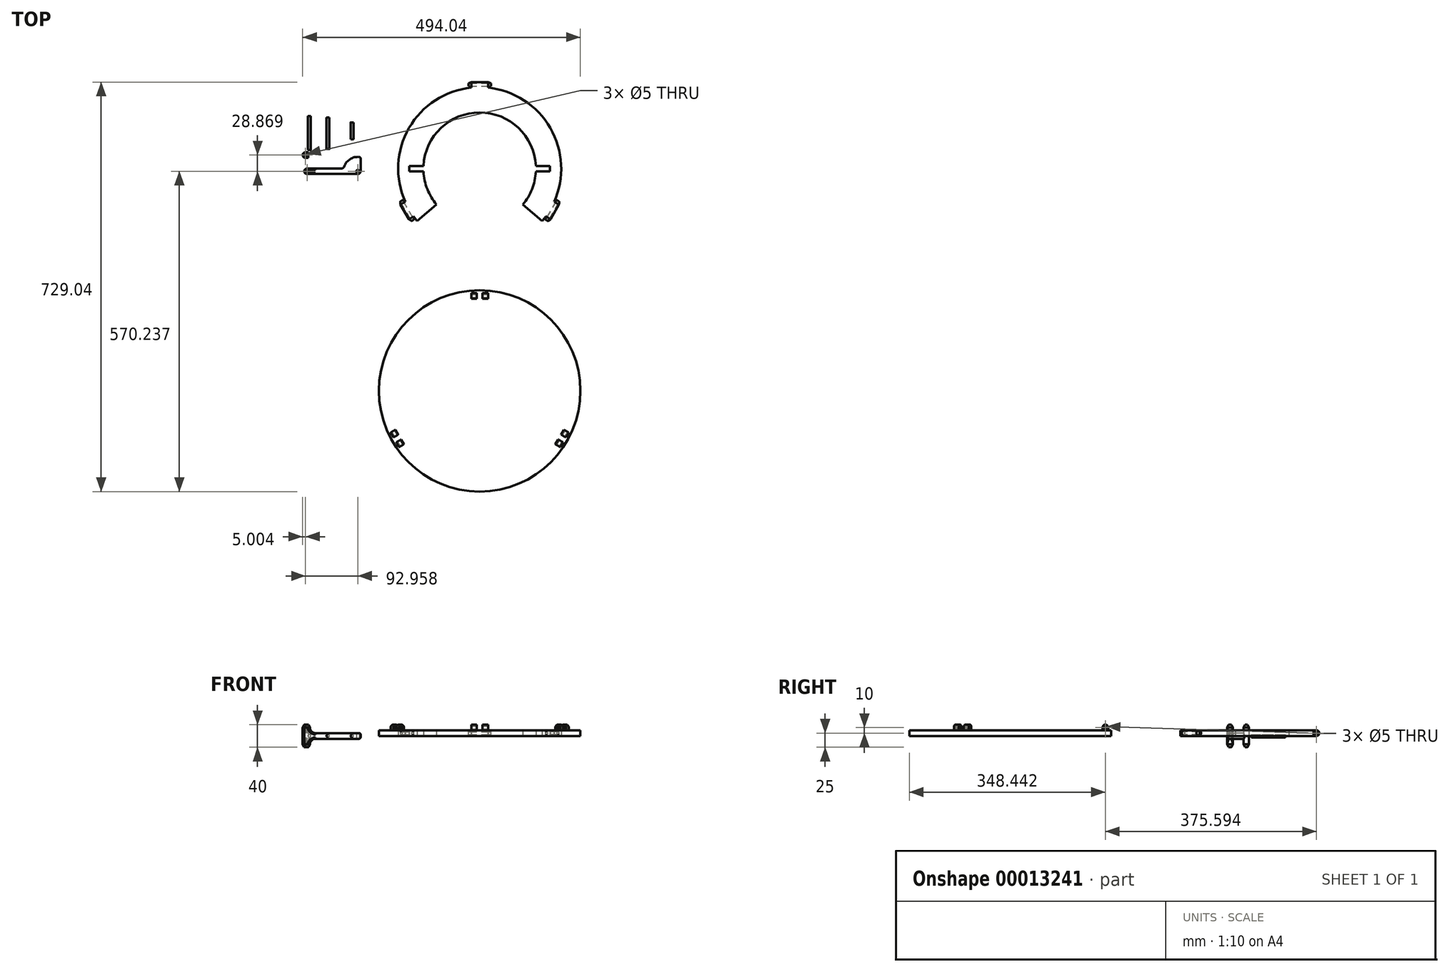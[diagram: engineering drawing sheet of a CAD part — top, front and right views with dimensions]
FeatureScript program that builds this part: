
annotation { "Feature Type Name" : "Feature", "Feature Type Description" : "" }
export const myFeature = defineFeature(function(context is Context, id is Id, definition is map)
    precondition{}
    {
        {
            var Q0;
            Q0=qCreatedBy(makeId("Top.planeOp"),FACE);
            var sketch = newSketch(context, id + "F0", { "sketchPlane" : qUnion([Q0])});
            skCircle(sketch, "E0", {"center": v(-58.2, 42.53) * mm, "radius": 2.5 * mm});
            skLineSegment(sketch, "E1", {"start": v(-53.2, 37.53) * mm, "end": v(-58.2, 37.53) * mm, "construction": true});
            skLineSegment(sketch, "E2", {"start": v(-148.2, 37.53) * mm, "end": v(-148.2, 47.53) * mm, "construction": true});
            skLineSegment(sketch, "E3", {"start": v(-148.2, 47.53) * mm, "end": v(-83.2, 47.53) * mm});
            skLineSegment(sketch, "E4", {"start": v(-83.2, 47.53) * mm, "end": v(-53.2, 67.53) * mm, "construction": true});
            skLineSegment(sketch, "E5", {"start": v(-53.2, 67.53) * mm, "end": v(-53.2, 42.53) * mm});
            skLineSegment(sketch, "E6", {"start": v(-53.2, 37.53) * mm, "end": v(-58.2, 42.53) * mm, "construction": true});
            skArc(sketch, "E7", {"start": v(-148.2, 47.53) * mm, "mid": v(-153.2, 42.53) * mm, "end": v(-148.2, 37.53) * mm});
            skArc(sketch, "E8", {"start": v(-53.2, 67.53) * mm, "mid": v(-72.34, 63.74) * mm, "end": v(-83.2, 47.53) * mm});
            skLineSegment(sketch, "E9", {"start": v(-148.2, 42.53) * mm, "end": v(-58.2, 42.53) * mm, "construction": true});
            skCircle(sketch, "E10", {"center": v(-148.2, 42.53) * mm, "radius": 2.5 * mm});
            skCircle(sketch, "E11", {"center": v(-148.2, 42.53) * mm, "radius": 5 * mm});
            skArc(sketch, "E12", {"start": v(-53.2, 42.53) * mm, "mid": v(-61.73, 46.06) * mm, "end": v(-58.2, 37.53) * mm, "construction": true});
            skArc(sketch, "E13", {"start": v(-58.2, 37.53) * mm, "mid": v(-54.66, 39) * mm, "end": v(-53.2, 42.53) * mm});
            skLineSegment(sketch, "E14", {"start": v(-53.2, 42.53) * mm, "end": v(-53.2, 37.53) * mm, "construction": true});
            skLineSegment(sketch, "E15", {"start": v(-58.2, 37.53) * mm, "end": v(-148.2, 37.53) * mm});
            skLineSegment(sketch, "E16.bottom", {"start": v(-111.22, 138) * mm, "end": v(-108.72, 138) * mm});
            skLineSegment(sketch, "E16.top", {"start": v(-111.22, 82) * mm, "end": v(-108.72, 82) * mm});
            skLineSegment(sketch, "E16.left", {"start": v(-111.22, 138) * mm, "end": v(-111.22, 82) * mm});
            skLineSegment(sketch, "E16.right", {"start": v(-108.72, 138) * mm, "end": v(-108.72, 82) * mm});
            skLineSegment(sketch, "E17", {"start": v(-148.2, 42.53) * mm, "end": v(-145.7, 42.53) * mm, "construction": true});
            skLineSegment(sketch, "E18", {"start": v(-58.2, 42.53) * mm, "end": v(-55.7, 42.53) * mm, "construction": true});
            skLineSegment(sketch, "E19.bottom", {"start": v(-68.32, 129.56) * mm, "end": v(-65.82, 129.56) * mm});
            skLineSegment(sketch, "E19.top", {"start": v(-68.32, 99.56) * mm, "end": v(-65.82, 99.56) * mm});
            skLineSegment(sketch, "E19.left", {"start": v(-68.32, 129.56) * mm, "end": v(-68.32, 99.56) * mm});
            skLineSegment(sketch, "E19.right", {"start": v(-65.82, 129.56) * mm, "end": v(-65.82, 99.56) * mm});
            skLineSegment(sketch, "E20.bottom", {"start": v(-144.15, 140.66) * mm, "end": v(-141.65, 140.66) * mm});
            skLineSegment(sketch, "E20.top", {"start": v(-144.15, 80.66) * mm, "end": v(-141.65, 80.66) * mm});
            skLineSegment(sketch, "E20.left", {"start": v(-144.15, 140.66) * mm, "end": v(-144.15, 80.66) * mm});
            skLineSegment(sketch, "E20.right", {"start": v(-141.65, 140.66) * mm, "end": v(-141.65, 80.66) * mm});
            skLineSegment(sketch, "E21.bottom", {"start": v(33.66, 52.1) * mm, "end": v(283.66, 52.1) * mm, "construction": true});
            skLineSegment(sketch, "E21.top", {"start": v(33.66, 42.1) * mm, "end": v(283.66, 42.1) * mm, "construction": true});
            skLineSegment(sketch, "E21.left", {"start": v(33.66, 52.1) * mm, "end": v(33.66, 42.1) * mm, "construction": true});
            skLineSegment(sketch, "E21.right", {"start": v(283.66, 52.1) * mm, "end": v(283.66, 42.1) * mm, "construction": true});
            skPoint(sketch, "E22", {"position": v(158.66, 47.1) * mm});
            skCircle(sketch, "E23", {"center": v(158.66, 47.1) * mm, "radius": 100 * mm});
            skCircle(sketch, "E24.cCircle", {"center": v(158.66, 47.1) * mm, "radius": 125.1 * mm, "construction": true});
            skCircle(sketch, "E25", {"center": v(158.66, 47.1) * mm, "radius": 145 * mm});
            skLineSegment(sketch, "E26", {"start": v(158.66, 47.1) * mm, "end": v(158.66, 192.1) * mm, "construction": true});
            skLineSegment(sketch, "E27", {"start": v(158.66, 47.1) * mm, "end": v(284.23, -25.4) * mm, "construction": true});
            skLineSegment(sketch, "E28", {"start": v(33.08, -25.4) * mm, "end": v(158.66, 47.1) * mm, "construction": true});
            skLineSegment(sketch, "E29.bottom", {"start": v(143.66, 201.33) * mm, "end": v(173.66, 201.33) * mm});
            skLineSegment(sketch, "E29.top", {"start": v(143.66, 191.33) * mm, "end": v(173.66, 191.33) * mm, "construction": true});
            skLineSegment(sketch, "E29.left", {"start": v(143.66, 201.33) * mm, "end": v(143.66, 191.33) * mm});
            skLineSegment(sketch, "E29.right", {"start": v(173.66, 201.33) * mm, "end": v(173.66, 191.33) * mm});
            skPoint(sketch, "E30", {"position": v(158.66, 191.33) * mm});
            skLineSegment(sketch, "E31.bottom", {"start": v(26.26, -12.02) * mm, "end": v(41.26, -38) * mm, "construction": true});
            skLineSegment(sketch, "E31.top", {"start": v(17.6, -17.02) * mm, "end": v(32.6, -43) * mm});
            skLineSegment(sketch, "E31.left", {"start": v(26.26, -12.02) * mm, "end": v(17.6, -17.02) * mm});
            skLineSegment(sketch, "E31.right", {"start": v(41.26, -38) * mm, "end": v(32.6, -43) * mm});
            skLineSegment(sketch, "E32.bottom", {"start": v(276.06, -38) * mm, "end": v(291.06, -12.02) * mm, "construction": true});
            skLineSegment(sketch, "E32.top", {"start": v(284.72, -43) * mm, "end": v(299.72, -17.02) * mm});
            skLineSegment(sketch, "E32.left", {"start": v(276.06, -38) * mm, "end": v(284.72, -43) * mm});
            skLineSegment(sketch, "E32.right", {"start": v(291.06, -12.02) * mm, "end": v(299.72, -17.02) * mm});
            skPoint(sketch, "E33", {"position": v(33.76, -25) * mm});
            skPoint(sketch, "E34", {"position": v(283.56, -25) * mm});
            skLineSegment(sketch, "E35", {"start": v(47.4, -45.89) * mm, "end": v(81.93, -17.03) * mm});
            skLineSegment(sketch, "E36", {"start": v(235.38, -17.03) * mm, "end": v(269.91, -45.89) * mm});
            skPoint(sketch, "E37", {"position": v(524.59, -60.45) * mm});
            skLineSegment(sketch, "E38", {"start": v(544.59, 16.73) * mm, "end": v(544.59, 116.73) * mm});
            skLineSegment(sketch, "E39", {"start": v(524.59, -60.45) * mm, "end": v(453.2, -60.45) * mm, "construction": true});
            skLineSegment(sketch, "E40", {"start": v(524.59, -60.45) * mm, "end": v(456.48, -1.62) * mm, "construction": true});
            skLineSegment(sketch, "E41", {"start": v(456.48, -1.62) * mm, "end": v(544.59, 16.73) * mm, "construction": true});
            skLineSegment(sketch, "E42", {"start": v(524.59, -60.45) * mm, "end": v(522.35, 29.52) * mm, "construction": true});
            skLineSegment(sketch, "E43", {"start": v(522.35, 29.52) * mm, "end": v(544.59, 116.73) * mm, "construction": true});
            skCircle(sketch, "E44", {"center": v(-151.16, 71.4) * mm, "radius": 5 * mm});
            skCircle(sketch, "E45", {"center": v(-151.16, 71.4) * mm, "radius": 2.5 * mm});
            skLineSegment(sketch, "E46.bottom", {"start": v(-151.16, 76.4) * mm, "end": v(-146.16, 76.4) * mm});
            skLineSegment(sketch, "E46.top", {"start": v(-151.16, 66.4) * mm, "end": v(-146.16, 66.4) * mm});
            skLineSegment(sketch, "E46.left", {"start": v(-151.16, 76.4) * mm, "end": v(-151.16, 66.4) * mm, "construction": true});
            skLineSegment(sketch, "E46.right", {"start": v(-146.16, 76.4) * mm, "end": v(-146.16, 66.4) * mm});
            skLineSegment(sketch, "E47", {"start": v(58.78, 52.1) * mm, "end": v(33.66, 52.1) * mm});
            skLineSegment(sketch, "E48", {"start": v(58.78, 42.1) * mm, "end": v(33.66, 42.1) * mm});
            skLineSegment(sketch, "E49", {"start": v(33.66, 42.1) * mm, "end": v(33.66, 52.1) * mm});
            skLineSegment(sketch, "E50", {"start": v(258.53, 52.1) * mm, "end": v(283.66, 52.1) * mm});
            skLineSegment(sketch, "E51", {"start": v(283.66, 42.1) * mm, "end": v(283.66, 52.1) * mm});
            skLineSegment(sketch, "E52", {"start": v(283.66, 42.1) * mm, "end": v(258.53, 42.1) * mm});
            skCircle(sketch, "E53", {"center": v(158.66, -348.5) * mm, "radius": 179.22 * mm});
            skLineSegment(sketch, "E54", {"start": v(143.66, 196.33) * mm, "end": v(173.66, 196.33) * mm, "construction": true});
            skLineSegment(sketch, "E55", {"start": v(158.66, 47.1) * mm, "end": v(158.66, 196.33) * mm, "construction": true});
            skLineSegment(sketch, "E56", {"start": v(158.66, -348.5) * mm, "end": v(158.66, -169.27) * mm, "construction": true});
            skLineSegment(sketch, "E57", {"start": v(143.66, -179.27) * mm, "end": v(173.66, -179.27) * mm, "construction": true});
            skLineSegment(sketch, "E58.bottom", {"start": v(143.66, -174.27) * mm, "end": v(153.66, -174.27) * mm});
            skLineSegment(sketch, "E58.top", {"start": v(143.66, -184.27) * mm, "end": v(153.66, -184.27) * mm});
            skLineSegment(sketch, "E58.left", {"start": v(143.66, -174.27) * mm, "end": v(143.66, -184.27) * mm});
            skLineSegment(sketch, "E58.right", {"start": v(153.66, -174.27) * mm, "end": v(153.66, -184.27) * mm});
            skLineSegment(sketch, "E59.bottom", {"start": v(163.66, -174.27) * mm, "end": v(173.66, -174.27) * mm});
            skLineSegment(sketch, "E59.top", {"start": v(163.66, -184.27) * mm, "end": v(173.66, -184.27) * mm});
            skLineSegment(sketch, "E59.left", {"start": v(163.66, -174.27) * mm, "end": v(163.66, -184.27) * mm});
            skLineSegment(sketch, "E59.right", {"start": v(173.66, -174.27) * mm, "end": v(173.66, -184.27) * mm});
            skPoint(sketch, "E60", {"position": v(158.66, -179.27) * mm});
            skLineSegment(sketch, "E61", {"start": v(158.66, -110.61) * mm, "end": v(307.88, -110.61) * mm, "construction": true});
            skLineSegment(sketch, "E62", {"start": v(307.88, -110.61) * mm, "end": v(327.88, -110.61) * mm, "construction": true});
            skLineSegment(sketch, "E63", {"start": v(524.59, -60.45) * mm, "end": v(544.59, -60.45) * mm, "construction": true});
            skLineSegment(sketch, "E64", {"start": v(158.66, -117.1) * mm, "end": v(327.88, -117.1) * mm, "construction": true});
            skLineSegment(sketch, "E65", {"start": v(158.66, -179.27) * mm, "end": v(158.66, -348.5) * mm, "construction": true});
            skLineSegment(sketch, "E66", {"start": v(158.66, -348.5) * mm, "end": v(305.2, -433.1) * mm, "construction": true});
            skLineSegment(sketch, "E67", {"start": v(12.1, -433.1) * mm, "end": v(158.66, -348.5) * mm, "construction": true});
            skLineSegment(sketch, "E68", {"start": v(297.7, -446.1) * mm, "end": v(312.7, -420.11) * mm, "construction": true});
            skLineSegment(sketch, "E69.bottom", {"start": v(303.38, -426.27) * mm, "end": v(308.38, -417.61) * mm});
            skLineSegment(sketch, "E69.top", {"start": v(312.04, -431.27) * mm, "end": v(317.04, -422.61) * mm});
            skLineSegment(sketch, "E69.left", {"start": v(303.38, -426.27) * mm, "end": v(312.04, -431.27) * mm});
            skLineSegment(sketch, "E69.right", {"start": v(308.38, -417.61) * mm, "end": v(317.04, -422.61) * mm});
            skLineSegment(sketch, "E70.bottom", {"start": v(298.38, -434.93) * mm, "end": v(307.04, -439.93) * mm});
            skLineSegment(sketch, "E70.top", {"start": v(293.38, -443.6) * mm, "end": v(302.04, -448.6) * mm});
            skLineSegment(sketch, "E70.left", {"start": v(298.38, -434.93) * mm, "end": v(293.38, -443.6) * mm});
            skLineSegment(sketch, "E70.right", {"start": v(307.04, -439.93) * mm, "end": v(302.04, -448.6) * mm});
            skLineSegment(sketch, "E71", {"start": v(4.6, -420.11) * mm, "end": v(19.6, -446.1) * mm, "construction": true});
            skLineSegment(sketch, "E72.bottom", {"start": v(18.94, -434.93) * mm, "end": v(23.94, -443.6) * mm});
            skLineSegment(sketch, "E72.top", {"start": v(10.28, -439.93) * mm, "end": v(15.28, -448.6) * mm});
            skLineSegment(sketch, "E72.left", {"start": v(23.94, -443.6) * mm, "end": v(15.28, -448.6) * mm});
            skLineSegment(sketch, "E72.right", {"start": v(18.94, -434.93) * mm, "end": v(10.28, -439.93) * mm});
            skLineSegment(sketch, "E73.bottom", {"start": v(8.94, -417.61) * mm, "end": v(13.94, -426.27) * mm});
            skLineSegment(sketch, "E73.top", {"start": v(0.28, -422.61) * mm, "end": v(5.28, -431.27) * mm});
            skLineSegment(sketch, "E73.left", {"start": v(13.94, -426.27) * mm, "end": v(5.28, -431.27) * mm});
            skLineSegment(sketch, "E73.right", {"start": v(8.94, -417.61) * mm, "end": v(0.28, -422.61) * mm});
            skSolve(sketch);
        }
        {
            var Q0;
            Q0=makeQuery(id+"F0.imprint","IMPRINT",FACE,{"disambiguationData":[TD([[makeQuery(id+"F0.imprint","IMPRINT",EDGE,{"derivedFrom":sQuery(id+"F0.wireOp",EDGE,"E0")}),-1.0]])]});
            var Q1;
            Q1=makeQuery(id+"F0.imprint","IMPRINT",FACE,{"disambiguationData":[TD([[makeQuery(id+"F0.imprint","IMPRINT",EDGE,{"derivedFrom":sQuery(id+"F0.wireOp",EDGE,"E10")}),-1.0]])]});
            extrude(context, id + "F1", {"entities" : qUnion([Q0, Q1]), "endBound" : BoundingType.SYMMETRIC, "depth" : 10 * mm});
        }
        {
            var Q0;
            Q0=makeQuery(id+"F0.imprint","IMPRINT",FACE,{"disambiguationData":[TD([[makeQuery(id+"F0.imprint","IMPRINT",EDGE,{"derivedFrom":sQuery(id+"F0.wireOp",EDGE,"E10")}),-1.0]])]});
            extrude(context, id + "F2", {"entities" : qUnion([Q0]), "operationType" : NewBodyOperationType.ADD, "endBound" : BoundingType.SYMMETRIC, "depth" : 30 * mm});
        }
        {
            var Q0;
            {var subQ0=sQuery(id+"F0.wireOp",EDGE,"E11");Q0=makeQuery(id+"F2.boolean.opBoolean","INTERSECT",EDGE,{"derivedFrom":[makeQuery(id+"F1.opExtrude","CAP_FACE",FACE,{"disambiguationData":[OSD([sQuery(id+"F0.wireOp",EDGE,"E0"),sQuery(id+"F0.wireOp",EDGE,"E3"),sQuery(id+"F0.wireOp",EDGE,"E5"),sQuery(id+"F0.wireOp",EDGE,"E8"),sQuery(id+"F0.wireOp",EDGE,"E10"),subQ0,sQuery(id+"F0.wireOp",EDGE,"E13"),sQuery(id+"F0.wireOp",EDGE,"E15")])],"isStart":false}),makeQuery(id+"F2.opExtrude","SWEPT_FACE",FACE,{"disambiguationData":[OSD([subQ0])]})]});}
            var Q1;
            {var subQ0=sQuery(id+"F0.wireOp",EDGE,"E11");Q1=makeQuery(id+"F2.boolean.opBoolean","INTERSECT",EDGE,{"derivedFrom":[makeQuery(id+"F1.opExtrude","CAP_FACE",FACE,{"disambiguationData":[OSD([sQuery(id+"F0.wireOp",EDGE,"E0"),sQuery(id+"F0.wireOp",EDGE,"E3"),sQuery(id+"F0.wireOp",EDGE,"E5"),sQuery(id+"F0.wireOp",EDGE,"E8"),sQuery(id+"F0.wireOp",EDGE,"E10"),subQ0,sQuery(id+"F0.wireOp",EDGE,"E13"),sQuery(id+"F0.wireOp",EDGE,"E15")])],"isStart":true}),makeQuery(id+"F2.opExtrude","SWEPT_FACE",FACE,{"disambiguationData":[OSD([subQ0])]})]});}
            fillet(context, id + "F3", {"entities" : qUnion([Q0, Q1]), "radius" : 10 * mm, "allowEdgeOverflow" : false});
        }
        {
            var Q0;
            Q0=makeQuery(id+"F1.opExtrude","SWEPT_EDGE",EDGE,{"disambiguationData":[OSD([sQuery(id+"F0.wireOp",EDGE,"E3"),sQuery(id+"F0.wireOp",EDGE,"E8")])]});
            fillet(context, id + "F4", {"entities" : qUnion([Q0]), "radius" : 5 * mm, "tangentPropagation" : true, "allowEdgeOverflow" : false});
        }
        {
            var Q0;
            Q0=makeQuery(id+"F1.opExtrude","CAP_EDGE",EDGE,{"disambiguationData":[OSD([sQuery(id+"F0.wireOp",EDGE,"E15")])],"isStart":false});
            var Q1;
            Q1=makeQuery(id+"F1.opExtrude","CAP_EDGE",EDGE,{"disambiguationData":[OSD([sQuery(id+"F0.wireOp",EDGE,"E8")])],"isStart":false});
            var Q2;
            Q2=makeQuery(id+"F1.opExtrude","CAP_EDGE",EDGE,{"disambiguationData":[OSD([sQuery(id+"F0.wireOp",EDGE,"E15")])],"isStart":true});
            var Q3;
            Q3=makeQuery(id+"F1.opExtrude","CAP_EDGE",EDGE,{"disambiguationData":[OSD([sQuery(id+"F0.wireOp",EDGE,"E3")])],"isStart":true});
            var Q4;
            Q4=makeQuery(id+"F1.opExtrude","SWEPT_EDGE",EDGE,{"disambiguationData":[OSD([sQuery(id+"F0.wireOp",EDGE,"E5"),sQuery(id+"F0.wireOp",EDGE,"E8")])]});
            fillet(context, id + "F5", {"entities" : qUnion([Q0, Q1, Q2, Q3, Q4]), "radius" : 2.5 * mm, "tangentPropagation" : true, "allowEdgeOverflow" : false});
        }
        {
            var Q0;
            Q0=makeQuery(id+"F2.opExtrude","CAP_FACE",FACE,{"disambiguationData":[OSD([sQuery(id+"F0.wireOp",EDGE,"E10"),sQuery(id+"F0.wireOp",EDGE,"E11")])],"isStart":false});
            extrude(context, id + "F6", {"entities" : qUnion([Q0]), "operationType" : NewBodyOperationType.ADD, "depth" : 5 * mm});
        }
        {
            var Q0;
            Q0=makeQuery(id+"F2.opExtrude","CAP_FACE",FACE,{"disambiguationData":[OSD([sQuery(id+"F0.wireOp",EDGE,"E10"),sQuery(id+"F0.wireOp",EDGE,"E11")])],"isStart":true});
            extrude(context, id + "F7", {"entities" : qUnion([Q0]), "operationType" : NewBodyOperationType.ADD, "depth" : 5 * mm});
        }
        {
            var Q0;
            Q0=makeQuery(id+"F6.opExtrude","CAP_EDGE",EDGE,{"disambiguationData":[OSD([sQuery(id+"F0.wireOp",EDGE,"E0"),sQuery(id+"F0.wireOp",EDGE,"E3"),sQuery(id+"F0.wireOp",EDGE,"E5"),sQuery(id+"F0.wireOp",EDGE,"E8"),sQuery(id+"F0.wireOp",EDGE,"E10"),sQuery(id+"F0.wireOp",EDGE,"E11"),sQuery(id+"F0.wireOp",EDGE,"E13"),sQuery(id+"F0.wireOp",EDGE,"E15")])],"isStart":false});
            var Q1;
            Q1=makeQuery(id+"F7.opExtrude","CAP_EDGE",EDGE,{"disambiguationData":[OSD([sQuery(id+"F0.wireOp",EDGE,"E0"),sQuery(id+"F0.wireOp",EDGE,"E3"),sQuery(id+"F0.wireOp",EDGE,"E5"),sQuery(id+"F0.wireOp",EDGE,"E8"),sQuery(id+"F0.wireOp",EDGE,"E10"),sQuery(id+"F0.wireOp",EDGE,"E11"),sQuery(id+"F0.wireOp",EDGE,"E13"),sQuery(id+"F0.wireOp",EDGE,"E15")])],"isStart":false});
            chamfer(context, id + "F8", {"entities" : qUnion([Q0, Q1]), "chamferType" : ChamferType.TWO_OFFSETS, "width1" : 2.5 * mm, "oppositeDirection" : false, "width2" : 5 * mm, "tangentPropagation" : true});
        }
        {
            var Q0;
            Q0=makeQuery(id+"F0.imprint","IMPRINT",FACE,{"disambiguationData":[TD([[makeQuery(id+"F0.imprint","IMPRINT",EDGE,{"derivedFrom":sQuery(id+"F0.wireOp",EDGE,"E20.bottom")}),-1.0]])]});
            var Q1;
            Q1=sQuery(id+"F0.wireOp",EDGE,"E20.left");
            revolve(context, id + "F9", {"entities" : qUnion([Q0]), "axis" : qUnion([Q1]), "revolveType" : RevolveType.FULL});
        }
        {
            var Q0;
            Q0=makeQuery(id+"F0.imprint","IMPRINT",FACE,{"disambiguationData":[TD([[makeQuery(id+"F0.imprint","IMPRINT",EDGE,{"derivedFrom":sQuery(id+"F0.wireOp",EDGE,"E16.bottom")}),-1.0]])]});
            var Q1;
            Q1=sQuery(id+"F0.wireOp",EDGE,"E16.left");
            revolve(context, id + "F10", {"entities" : qUnion([Q0]), "axis" : qUnion([Q1]), "revolveType" : RevolveType.FULL});
        }
        {
            var Q0;
            Q0=makeQuery(id+"F0.imprint","IMPRINT",FACE,{"disambiguationData":[TD([[makeQuery(id+"F0.imprint","IMPRINT",EDGE,{"derivedFrom":sQuery(id+"F0.wireOp",EDGE,"E19.bottom")}),-1.0]])]});
            var Q1;
            Q1=sQuery(id+"F0.wireOp",EDGE,"E19.left");
            revolve(context, id + "F11", {"entities" : qUnion([Q0]), "axis" : qUnion([Q1]), "revolveType" : RevolveType.FULL});
        }
        {
            var Q0;
            Q0=makeQuery(id+"F0.imprint","IMPRINT",FACE,{"disambiguationData":[TD([[makeQuery(id+"F0.imprint","IMPRINT",EDGE,{"derivedFrom":sQuery(id+"F0.wireOp",EDGE,"E45")}),-1.0]])]});
            var Q1;
            {var subQ3=sQuery(id+"F0.wireOp",EDGE,"E46.top");Q1=makeQuery(id+"F0.imprint","IMPRINT",FACE,{"disambiguationData":[TD([[makeQuery(id+"F0.imprint","IMPRINT",EDGE,{"derivedFrom":subQ3}),1.0]])]});}
            var Q2;
            {var subQ3=sQuery(id+"F0.wireOp",EDGE,"E46.bottom");Q2=makeQuery(id+"F0.imprint","IMPRINT",FACE,{"disambiguationData":[TD([[makeQuery(id+"F0.imprint","IMPRINT",EDGE,{"derivedFrom":subQ3}),-1.0]])]});}
            extrude(context, id + "F12", {"entities" : qUnion([Q0, Q1, Q2]), "endBound" : BoundingType.SYMMETRIC, "depth" : 30 * mm});
        }
        {
            var Q0;
            Q0=makeQuery(id+"F0.imprint","IMPRINT",FACE,{"disambiguationData":[TD([[makeQuery(id+"F0.imprint","IMPRINT",EDGE,{"derivedFrom":sQuery(id+"F0.wireOp",EDGE,"E45")}),-1.0]])]});
            extrude(context, id + "F13", {"entities" : qUnion([Q0]), "operationType" : NewBodyOperationType.ADD, "endBound" : BoundingType.SYMMETRIC, "depth" : 40 * mm});
        }
        {
            var Q0;
            Q0=makeQuery(id+"F13.opExtrude","CAP_EDGE",EDGE,{"disambiguationData":[OSD([sQuery(id+"F0.wireOp",EDGE,"E44")])],"isStart":true});
            var Q1;
            Q1=makeQuery(id+"F13.opExtrude","CAP_EDGE",EDGE,{"disambiguationData":[OSD([sQuery(id+"F0.wireOp",EDGE,"E44")])],"isStart":false});
            chamfer(context, id + "F14", {"entities" : qUnion([Q0, Q1]), "chamferType" : ChamferType.TWO_OFFSETS, "width1" : 2.6 * mm, "oppositeDirection" : true, "width2" : 5 * mm, "tangentPropagation" : true});
        }
        {
            var Q0;
            Q0=makeQuery(id+"F0.imprint","IMPRINT",FACE,{"disambiguationData":[TD([[makeQuery(id+"F0.imprint","IMPRINT",EDGE,{"derivedFrom":sQuery(id+"F0.wireOp",EDGE,"E53")}),1.0]])]});
            extrude(context, id + "F15", {"entities" : qUnion([Q0]), "depth" : 10 * mm});
        }
        {
            var Q0;
            Q0=makeQuery(id+"F0.imprint","IMPRINT",FACE,{"disambiguationData":[TD([[makeQuery(id+"F0.imprint","IMPRINT",EDGE,{"derivedFrom":sQuery(id+"F0.wireOp",EDGE,"E72.bottom")}),-1.0]])]});
            var Q1;
            Q1=makeQuery(id+"F0.imprint","IMPRINT",FACE,{"disambiguationData":[TD([[makeQuery(id+"F0.imprint","IMPRINT",EDGE,{"derivedFrom":sQuery(id+"F0.wireOp",EDGE,"E73.bottom")}),-1.0]])]});
            var Q2;
            Q2=makeQuery(id+"F0.imprint","IMPRINT",FACE,{"disambiguationData":[TD([[makeQuery(id+"F0.imprint","IMPRINT",EDGE,{"derivedFrom":sQuery(id+"F0.wireOp",EDGE,"E58.bottom")}),-1.0]])]});
            var Q3;
            Q3=makeQuery(id+"F0.imprint","IMPRINT",FACE,{"disambiguationData":[TD([[makeQuery(id+"F0.imprint","IMPRINT",EDGE,{"derivedFrom":sQuery(id+"F0.wireOp",EDGE,"E59.bottom")}),-1.0]])]});
            var Q4;
            Q4=makeQuery(id+"F0.imprint","IMPRINT",FACE,{"disambiguationData":[TD([[makeQuery(id+"F0.imprint","IMPRINT",EDGE,{"derivedFrom":sQuery(id+"F0.wireOp",EDGE,"E70.bottom")}),-1.0]])]});
            var Q5;
            Q5=makeQuery(id+"F0.imprint","IMPRINT",FACE,{"disambiguationData":[TD([[makeQuery(id+"F0.imprint","IMPRINT",EDGE,{"derivedFrom":sQuery(id+"F0.wireOp",EDGE,"E69.bottom")}),-1.0]])]});
            extrude(context, id + "F16", {"entities" : qUnion([Q0, Q1, Q2, Q3, Q4, Q5]), "operationType" : NewBodyOperationType.ADD, "depth" : 20 * mm});
        }
        {
            var Q0;
            Q0=makeQuery(id+"F16.opExtrude","SWEPT_FACE",FACE,{"disambiguationData":[OSD([sQuery(id+"F0.wireOp",EDGE,"E70.top")])]});
            var sketch = newSketch(context, id + "F17", { "sketchPlane" : qUnion([Q0])});
            skPoint(sketch, "E74.0", {"position": v(475.87, 20) * mm});
            skPoint(sketch, "E75.0", {"position": v(485.87, 20) * mm});
            skPoint(sketch, "E76.0", {"position": v(485.87, 10) * mm});
            skCircle(sketch, "E77", {"center": v(480.87, 15) * mm, "radius": 5 * mm});
            skLineSegment(sketch, "E78.bottom", {"start": v(475.87, 20) * mm, "end": v(485.87, 20) * mm});
            skLineSegment(sketch, "E78.top", {"start": v(475.87, 10) * mm, "end": v(485.87, 10) * mm});
            skLineSegment(sketch, "E78.left", {"start": v(475.87, 20) * mm, "end": v(475.87, 10) * mm});
            skLineSegment(sketch, "E78.right", {"start": v(485.87, 20) * mm, "end": v(485.87, 10) * mm});
            skCircle(sketch, "E79", {"center": v(480.87, 15) * mm, "radius": 2.5 * mm});
            skSolve(sketch);
        }
        {
            var Q0;
            {var subQ1=sQuery(id+"F17.wireOp",EDGE,"E77");var subQ3=sQuery(id+"F17.wireOp",EDGE,"E78.bottom");var subQ5=makeQuery(id+"F17.imprint","INTERSECT",VERTEX,{"derivedFrom":[subQ1,subQ3]});Q0=makeQuery(id+"F17.imprint","IMPRINT",FACE,{"disambiguationData":[TD([[makeQuery(id+"F17.imprint","IMPRINT",EDGE,{"disambiguationData":[TD([[subQ5,1.0]])],"derivedFrom":subQ1}),-1.0]])]});}
            var Q1;
            {var subQ1=sQuery(id+"F17.wireOp",EDGE,"E77");var subQ3=sQuery(id+"F17.wireOp",EDGE,"E78.bottom");var subQ5=makeQuery(id+"F17.imprint","INTERSECT",VERTEX,{"derivedFrom":[subQ1,subQ3]});Q1=makeQuery(id+"F17.imprint","IMPRINT",FACE,{"disambiguationData":[TD([[makeQuery(id+"F17.imprint","IMPRINT",EDGE,{"disambiguationData":[TD([[subQ5,-1.0]])],"derivedFrom":subQ1}),-1.0]])]});}
            var Q2;
            Q2=makeQuery(id+"F17.imprint","IMPRINT",FACE,{"disambiguationData":[TD([[makeQuery(id+"F17.imprint","IMPRINT",EDGE,{"derivedFrom":sQuery(id+"F17.wireOp",EDGE,"E79")}),1.0]])]});
            var Q3;
            Q3=makeQuery(id+"F16.opExtrude","SWEPT_FACE",FACE,{"disambiguationData":[OSD([sQuery(id+"F0.wireOp",EDGE,"E69.right")])]});
            extrude(context, id + "F18", {"entities" : qUnion([Q0, Q1, Q2]), "operationType" : NewBodyOperationType.REMOVE, "endBound" : BoundingType.UP_TO_SURFACE, "oppositeDirection" : true, "endBoundEntityFace" : qUnion([Q3]), "depth" : 25 * mm});
        }
        {
            var Q0;
            Q0=makeQuery(id+"F16.opExtrude","SWEPT_FACE",FACE,{"disambiguationData":[OSD([sQuery(id+"F0.wireOp",EDGE,"E59.right")])]});
            var sketch = newSketch(context, id + "F19", { "sketchPlane" : qUnion([Q0])});
            skLineSegment(sketch, "E80.0.0", {"start": v(-184.27, 10) * mm, "end": v(-174.27, 10) * mm});
            skLineSegment(sketch, "E80.0.1", {"start": v(-174.27, 10) * mm, "end": v(-174.27, 20) * mm});
            skLineSegment(sketch, "E80.0.2", {"start": v(-174.27, 20) * mm, "end": v(-184.27, 20) * mm});
            skLineSegment(sketch, "E80.0.3", {"start": v(-184.27, 20) * mm, "end": v(-184.27, 10) * mm});
            skCircle(sketch, "E81", {"center": v(-179.27, 15) * mm, "radius": 5 * mm});
            skCircle(sketch, "E82", {"center": v(-179.27, 15) * mm, "radius": 2.5 * mm});
            skSolve(sketch);
        }
        {
            var Q0;
            Q0=makeQuery(id+"F19.imprint","IMPRINT",FACE,{"disambiguationData":[TD([[makeQuery(id+"F19.imprint","IMPRINT",EDGE,{"derivedFrom":sQuery(id+"F19.wireOp",EDGE,"E82")}),1.0]])]});
            var Q1;
            {var subQ1=sQuery(id+"F19.wireOp",EDGE,"E80.0.3");var subQ3=sQuery(id+"F19.wireOp",EDGE,"E80.0.2");var subQ5=makeQuery(id+"F19.imprint","INTERSECT",VERTEX,{"derivedFrom":[subQ3,subQ1]});Q1=makeQuery(id+"F19.imprint","IMPRINT",FACE,{"disambiguationData":[TD([[makeQuery(id+"F19.imprint","IMPRINT",EDGE,{"disambiguationData":[TD([[subQ5,1.0]])],"derivedFrom":subQ3}),1.0]])]});}
            var Q2;
            {var subQ0=sQuery(id+"F19.wireOp",EDGE,"E80.0.2");var subQ3=sQuery(id+"F19.wireOp",EDGE,"E80.0.1");var subQ4=makeQuery(id+"F19.imprint","INTERSECT",VERTEX,{"derivedFrom":[subQ3,subQ0]});Q2=makeQuery(id+"F19.imprint","IMPRINT",FACE,{"disambiguationData":[TD([[makeQuery(id+"F19.imprint","IMPRINT",EDGE,{"disambiguationData":[TD([[subQ4,-1.0]])],"derivedFrom":subQ3}),-1.0]])]});}
            var Q3;
            Q3=makeQuery(id+"F16.opExtrude","SWEPT_FACE",FACE,{"disambiguationData":[OSD([sQuery(id+"F0.wireOp",EDGE,"E58.left")])]});
            extrude(context, id + "F20", {"entities" : qUnion([Q0, Q1, Q2]), "operationType" : NewBodyOperationType.REMOVE, "endBound" : BoundingType.UP_TO_SURFACE, "oppositeDirection" : true, "endBoundEntityFace" : qUnion([Q3]), "depth" : 25 * mm});
        }
        {
            var Q0;
            Q0=makeQuery(id+"F16.opExtrude","SWEPT_FACE",FACE,{"disambiguationData":[OSD([sQuery(id+"F0.wireOp",EDGE,"E72.left")])]});
            var sketch = newSketch(context, id + "F21", { "sketchPlane" : qUnion([Q0])});
            skLineSegment(sketch, "E83.0.0", {"start": v(-211.07, 10) * mm, "end": v(-201.07, 10) * mm});
            skLineSegment(sketch, "E83.0.1", {"start": v(-201.07, 10) * mm, "end": v(-201.07, 20) * mm});
            skLineSegment(sketch, "E83.0.2", {"start": v(-201.07, 20) * mm, "end": v(-211.07, 20) * mm});
            skLineSegment(sketch, "E83.0.3", {"start": v(-211.07, 20) * mm, "end": v(-211.07, 10) * mm});
            skCircle(sketch, "E84", {"center": v(-206.07, 15) * mm, "radius": 5 * mm});
            skCircle(sketch, "E85", {"center": v(-206.07, 15) * mm, "radius": 2.5 * mm});
            skSolve(sketch);
        }
        {
            var Q0;
            Q0=makeQuery(id+"F21.imprint","IMPRINT",FACE,{"disambiguationData":[TD([[makeQuery(id+"F21.imprint","IMPRINT",EDGE,{"derivedFrom":sQuery(id+"F21.wireOp",EDGE,"E85")}),1.0]])]});
            var Q1;
            {var subQ1=sQuery(id+"F21.wireOp",EDGE,"E83.0.3");var subQ3=sQuery(id+"F21.wireOp",EDGE,"E83.0.2");var subQ5=makeQuery(id+"F21.imprint","INTERSECT",VERTEX,{"derivedFrom":[subQ3,subQ1]});Q1=makeQuery(id+"F21.imprint","IMPRINT",FACE,{"disambiguationData":[TD([[makeQuery(id+"F21.imprint","IMPRINT",EDGE,{"disambiguationData":[TD([[subQ5,1.0]])],"derivedFrom":subQ3}),1.0]])]});}
            var Q2;
            {var subQ1=sQuery(id+"F21.wireOp",EDGE,"E83.0.2");var subQ3=sQuery(id+"F21.wireOp",EDGE,"E83.0.1");var subQ5=makeQuery(id+"F21.imprint","INTERSECT",VERTEX,{"derivedFrom":[subQ3,subQ1]});Q2=makeQuery(id+"F21.imprint","IMPRINT",FACE,{"disambiguationData":[TD([[makeQuery(id+"F21.imprint","IMPRINT",EDGE,{"disambiguationData":[TD([[subQ5,-1.0]])],"derivedFrom":subQ3}),-1.0]])]});}
            var Q3;
            Q3=makeQuery(id+"F16.opExtrude","SWEPT_FACE",FACE,{"disambiguationData":[OSD([sQuery(id+"F0.wireOp",EDGE,"E73.right")])]});
            extrude(context, id + "F22", {"entities" : qUnion([Q0, Q1, Q2]), "operationType" : NewBodyOperationType.REMOVE, "endBound" : BoundingType.UP_TO_SURFACE, "oppositeDirection" : true, "endBoundEntityFace" : qUnion([Q3]), "depth" : 25 * mm});
        }
        {
            var Q0;
            {var subQ4=sQuery(id+"F0.wireOp",EDGE,"E35");Q0=makeQuery(id+"F0.imprint","IMPRINT",FACE,{"disambiguationData":[TD([[makeQuery(id+"F0.imprint","IMPRINT",EDGE,{"derivedFrom":subQ4}),1.0]])]});}
            var Q1;
            Q1=makeQuery(id+"F0.imprint","IMPRINT",FACE,{"disambiguationData":[TD([[makeQuery(id+"F0.imprint","IMPRINT",EDGE,{"derivedFrom":sQuery(id+"F0.wireOp",EDGE,"E31.top")}),1.0]])]});
            var Q2;
            Q2=makeQuery(id+"F0.imprint","IMPRINT",FACE,{"disambiguationData":[TD([[makeQuery(id+"F0.imprint","IMPRINT",EDGE,{"derivedFrom":sQuery(id+"F0.wireOp",EDGE,"E32.top")}),1.0]])]});
            var Q3;
            Q3=makeQuery(id+"F0.imprint","IMPRINT",FACE,{"disambiguationData":[TD([[makeQuery(id+"F0.imprint","IMPRINT",EDGE,{"derivedFrom":sQuery(id+"F0.wireOp",EDGE,"E29.bottom")}),-1.0]])]});
            extrude(context, id + "F23", {"entities" : qUnion([Q0, Q1, Q2, Q3]), "depth" : 10 * mm});
        }
        {
            var Q0;
            Q0=makeQuery(id+"F23.opExtrude","SWEPT_FACE",FACE,{"disambiguationData":[OSD([sQuery(id+"F0.wireOp",EDGE,"E31.right")])]});
            var sketch = newSketch(context, id + "F24", { "sketchPlane" : qUnion([Q0])});
            skLineSegment(sketch, "E86.0.0", {"start": v(6.73, 0) * mm, "end": v(16.73, 0) * mm});
            skLineSegment(sketch, "E86.0.1", {"start": v(16.73, 0) * mm, "end": v(16.73, 10) * mm});
            skLineSegment(sketch, "E86.0.2", {"start": v(16.73, 10) * mm, "end": v(6.73, 10) * mm});
            skLineSegment(sketch, "E86.0.3", {"start": v(6.73, 10) * mm, "end": v(6.73, 0) * mm});
            skCircle(sketch, "E87", {"center": v(11.73, 5) * mm, "radius": 5 * mm});
            skCircle(sketch, "E88", {"center": v(11.73, 5) * mm, "radius": 2.5 * mm});
            skSolve(sketch);
        }
        {
            var Q0;
            Q0=makeQuery(id+"F24.imprint","IMPRINT",FACE,{"disambiguationData":[TD([[makeQuery(id+"F24.imprint","IMPRINT",EDGE,{"derivedFrom":sQuery(id+"F24.wireOp",EDGE,"E88")}),1.0]])]});
            var Q1;
            {var subQ1=sQuery(id+"F24.wireOp",EDGE,"E86.0.3");var subQ3=sQuery(id+"F24.wireOp",EDGE,"E86.0.2");var subQ5=makeQuery(id+"F24.imprint","INTERSECT",VERTEX,{"derivedFrom":[subQ3,subQ1]});Q1=makeQuery(id+"F24.imprint","IMPRINT",FACE,{"disambiguationData":[TD([[makeQuery(id+"F24.imprint","IMPRINT",EDGE,{"disambiguationData":[TD([[subQ5,1.0]])],"derivedFrom":subQ3}),1.0]])]});}
            var Q2;
            {var subQ1=sQuery(id+"F24.wireOp",EDGE,"E86.0.3");var subQ3=sQuery(id+"F24.wireOp",EDGE,"E86.0.0");var subQ5=makeQuery(id+"F24.imprint","INTERSECT",VERTEX,{"derivedFrom":[subQ3,subQ1]});Q2=makeQuery(id+"F24.imprint","IMPRINT",FACE,{"disambiguationData":[TD([[makeQuery(id+"F24.imprint","IMPRINT",EDGE,{"disambiguationData":[TD([[subQ5,1.0]])],"derivedFrom":subQ3}),-1.0]])]});}
            var Q3;
            Q3=makeQuery(id+"F23.opExtrude","SWEPT_FACE",FACE,{"disambiguationData":[OSD([sQuery(id+"F0.wireOp",EDGE,"E31.left")])]});
            extrude(context, id + "F25", {"entities" : qUnion([Q0, Q1, Q2]), "operationType" : NewBodyOperationType.REMOVE, "endBound" : BoundingType.UP_TO_SURFACE, "oppositeDirection" : true, "endBoundEntityFace" : qUnion([Q3]), "depth" : 25 * mm});
        }
        {
            var Q0;
            Q0=makeQuery(id+"F23.opExtrude","SWEPT_FACE",FACE,{"disambiguationData":[OSD([sQuery(id+"F0.wireOp",EDGE,"E32.left")])]});
            var sketch = newSketch(context, id + "F26", { "sketchPlane" : qUnion([Q0])});
            skLineSegment(sketch, "E89.0.0", {"start": v(258.07, 0) * mm, "end": v(268.07, 0) * mm});
            skLineSegment(sketch, "E89.0.1", {"start": v(268.07, 0) * mm, "end": v(268.07, 10) * mm});
            skLineSegment(sketch, "E89.0.2", {"start": v(268.07, 10) * mm, "end": v(258.07, 10) * mm});
            skLineSegment(sketch, "E89.0.3", {"start": v(258.07, 10) * mm, "end": v(258.07, 0) * mm});
            skCircle(sketch, "E90", {"center": v(263.07, 5) * mm, "radius": 5 * mm});
            skCircle(sketch, "E91", {"center": v(263.07, 5) * mm, "radius": 2.5 * mm});
            skSolve(sketch);
        }
        {
            var Q0;
            {var subQ1=sQuery(id+"F26.wireOp",EDGE,"E89.0.2");var subQ3=sQuery(id+"F26.wireOp",EDGE,"E89.0.1");var subQ5=makeQuery(id+"F26.imprint","INTERSECT",VERTEX,{"derivedFrom":[subQ3,subQ1]});Q0=makeQuery(id+"F26.imprint","IMPRINT",FACE,{"disambiguationData":[TD([[makeQuery(id+"F26.imprint","IMPRINT",EDGE,{"disambiguationData":[TD([[subQ5,-1.0]])],"derivedFrom":subQ3}),-1.0]])]});}
            var Q1;
            {var subQ1=sQuery(id+"F26.wireOp",EDGE,"E89.0.1");var subQ3=sQuery(id+"F26.wireOp",EDGE,"E89.0.0");var subQ5=makeQuery(id+"F26.imprint","INTERSECT",VERTEX,{"derivedFrom":[subQ3,subQ1]});Q1=makeQuery(id+"F26.imprint","IMPRINT",FACE,{"disambiguationData":[TD([[makeQuery(id+"F26.imprint","IMPRINT",EDGE,{"disambiguationData":[TD([[subQ5,1.0]])],"derivedFrom":subQ3}),1.0]])]});}
            var Q2;
            Q2=makeQuery(id+"F26.imprint","IMPRINT",FACE,{"disambiguationData":[TD([[makeQuery(id+"F26.imprint","IMPRINT",EDGE,{"derivedFrom":sQuery(id+"F26.wireOp",EDGE,"E91")}),1.0]])]});
            var Q3;
            Q3=makeQuery(id+"F23.opExtrude","SWEPT_FACE",FACE,{"disambiguationData":[OSD([sQuery(id+"F0.wireOp",EDGE,"E32.right")])]});
            extrude(context, id + "F27", {"entities" : qUnion([Q0, Q1, Q2]), "operationType" : NewBodyOperationType.REMOVE, "endBound" : BoundingType.UP_TO_SURFACE, "oppositeDirection" : true, "endBoundEntityFace" : qUnion([Q3]), "depth" : 25 * mm});
        }
        {
            var Q0;
            Q0=makeQuery(id+"F23.opExtrude","SWEPT_FACE",FACE,{"disambiguationData":[OSD([sQuery(id+"F0.wireOp",EDGE,"E29.right")])]});
            var sketch = newSketch(context, id + "F28", { "sketchPlane" : qUnion([Q0])});
            skLineSegment(sketch, "E92.0.0", {"start": v(191.33, 0) * mm, "end": v(201.33, 0) * mm});
            skLineSegment(sketch, "E92.0.1", {"start": v(201.33, 0) * mm, "end": v(201.33, 10) * mm});
            skLineSegment(sketch, "E92.0.2", {"start": v(201.33, 10) * mm, "end": v(191.33, 10) * mm});
            skLineSegment(sketch, "E92.0.3", {"start": v(191.33, 10) * mm, "end": v(191.33, 0) * mm});
            skCircle(sketch, "E93", {"center": v(196.33, 5) * mm, "radius": 5 * mm});
            skCircle(sketch, "E94", {"center": v(196.33, 5) * mm, "radius": 2.5 * mm});
            skSolve(sketch);
        }
        {
            var Q0;
            Q0=makeQuery(id+"F28.imprint","IMPRINT",FACE,{"disambiguationData":[TD([[makeQuery(id+"F28.imprint","IMPRINT",EDGE,{"derivedFrom":sQuery(id+"F28.wireOp",EDGE,"E94")}),1.0]])]});
            var Q1;
            {var subQ1=sQuery(id+"F28.wireOp",EDGE,"E92.0.2");var subQ3=sQuery(id+"F28.wireOp",EDGE,"E92.0.1");var subQ5=makeQuery(id+"F28.imprint","INTERSECT",VERTEX,{"derivedFrom":[subQ3,subQ1]});Q1=makeQuery(id+"F28.imprint","IMPRINT",FACE,{"disambiguationData":[TD([[makeQuery(id+"F28.imprint","IMPRINT",EDGE,{"disambiguationData":[TD([[subQ5,-1.0]])],"derivedFrom":subQ3}),-1.0]])]});}
            var Q2;
            {var subQ0=sQuery(id+"F28.wireOp",EDGE,"E92.0.1");var subQ3=sQuery(id+"F28.wireOp",EDGE,"E92.0.0");var subQ4=makeQuery(id+"F28.imprint","INTERSECT",VERTEX,{"derivedFrom":[subQ3,subQ0]});Q2=makeQuery(id+"F28.imprint","IMPRINT",FACE,{"disambiguationData":[TD([[makeQuery(id+"F28.imprint","IMPRINT",EDGE,{"disambiguationData":[TD([[subQ4,-1.0]])],"derivedFrom":subQ3}),-1.0]])]});}
            var Q3;
            Q3=makeQuery(id+"F23.opExtrude","SWEPT_FACE",FACE,{"disambiguationData":[OSD([sQuery(id+"F0.wireOp",EDGE,"E29.left")])]});
            extrude(context, id + "F29", {"entities" : qUnion([Q0, Q1, Q2]), "operationType" : NewBodyOperationType.REMOVE, "endBound" : BoundingType.UP_TO_SURFACE, "oppositeDirection" : true, "endBoundEntityFace" : qUnion([Q3]), "depth" : 25 * mm});
        }
        {
            var Q0;
            Q0=makeQuery(id+"F24.imprint","IMPRINT",FACE,{"disambiguationData":[TD([[makeQuery(id+"F24.imprint","IMPRINT",EDGE,{"derivedFrom":sQuery(id+"F24.wireOp",EDGE,"E88")}),-1.0]])]});
            extrude(context, id + "F30", {"entities" : qUnion([Q0]), "operationType" : NewBodyOperationType.ADD, "depth" : 5 * mm, "hasSecondDirection" : true, "secondDirectionOppositeDirection" : true, "secondDirectionDepth" : 35 * mm});
        }
        {
            var Q0;
            Q0=makeQuery(id+"F26.imprint","IMPRINT",FACE,{"disambiguationData":[TD([[makeQuery(id+"F26.imprint","IMPRINT",EDGE,{"derivedFrom":sQuery(id+"F26.wireOp",EDGE,"E91")}),-1.0]])]});
            extrude(context, id + "F31", {"entities" : qUnion([Q0]), "operationType" : NewBodyOperationType.ADD, "depth" : 5 * mm, "hasSecondDirection" : true, "secondDirectionOppositeDirection" : true, "secondDirectionDepth" : 35 * mm});
        }
        {
            var Q0;
            Q0=makeQuery(id+"F28.imprint","IMPRINT",FACE,{"disambiguationData":[TD([[makeQuery(id+"F28.imprint","IMPRINT",EDGE,{"derivedFrom":sQuery(id+"F28.wireOp",EDGE,"E94")}),-1.0]])]});
            extrude(context, id + "F32", {"entities" : qUnion([Q0]), "operationType" : NewBodyOperationType.ADD, "depth" : 5 * mm, "hasSecondDirection" : true, "secondDirectionOppositeDirection" : true, "secondDirectionDepth" : 35 * mm});
        }
        {
            var Q0;
            Q0=makeQuery(id+"F30.opExtrude","CAP_EDGE",EDGE,{"disambiguationData":[OSD([sQuery(id+"F24.wireOp",EDGE,"E87")])],"isStart":false});
            var Q1;
            Q1=makeQuery(id+"F30.opExtrude","CAP_EDGE",EDGE,{"disambiguationData":[OSD([sQuery(id+"F24.wireOp",EDGE,"E87")])],"isStart":true});
            var Q2;
            Q2=makeQuery(id+"F32.opExtrude","CAP_EDGE",EDGE,{"disambiguationData":[OSD([sQuery(id+"F28.wireOp",EDGE,"E93")])],"isStart":false});
            var Q3;
            Q3=makeQuery(id+"F31.opExtrude","CAP_EDGE",EDGE,{"disambiguationData":[OSD([sQuery(id+"F26.wireOp",EDGE,"E90")])],"isStart":false});
            chamfer(context, id + "F33", {"entities" : qUnion([Q0, Q1, Q2, Q3]), "chamferType" : ChamferType.TWO_OFFSETS, "width1" : 2.5 * mm, "oppositeDirection" : false, "width2" : 5 * mm, "tangentPropagation" : true});
        }
        {
            var Q0;
            Q0=makeQuery(id+"F31.opExtrude","CAP_EDGE",EDGE,{"disambiguationData":[OSD([sQuery(id+"F26.wireOp",EDGE,"E90")])],"isStart":true});
            var Q1;
            Q1=makeQuery(id+"F32.opExtrude","CAP_EDGE",EDGE,{"disambiguationData":[OSD([sQuery(id+"F28.wireOp",EDGE,"E93")])],"isStart":true});
            chamfer(context, id + "F34", {"entities" : qUnion([Q0, Q1]), "chamferType" : ChamferType.TWO_OFFSETS, "width1" : 2.5 * mm, "oppositeDirection" : true, "width2" : 5 * mm, "tangentPropagation" : true});
        }
    });
